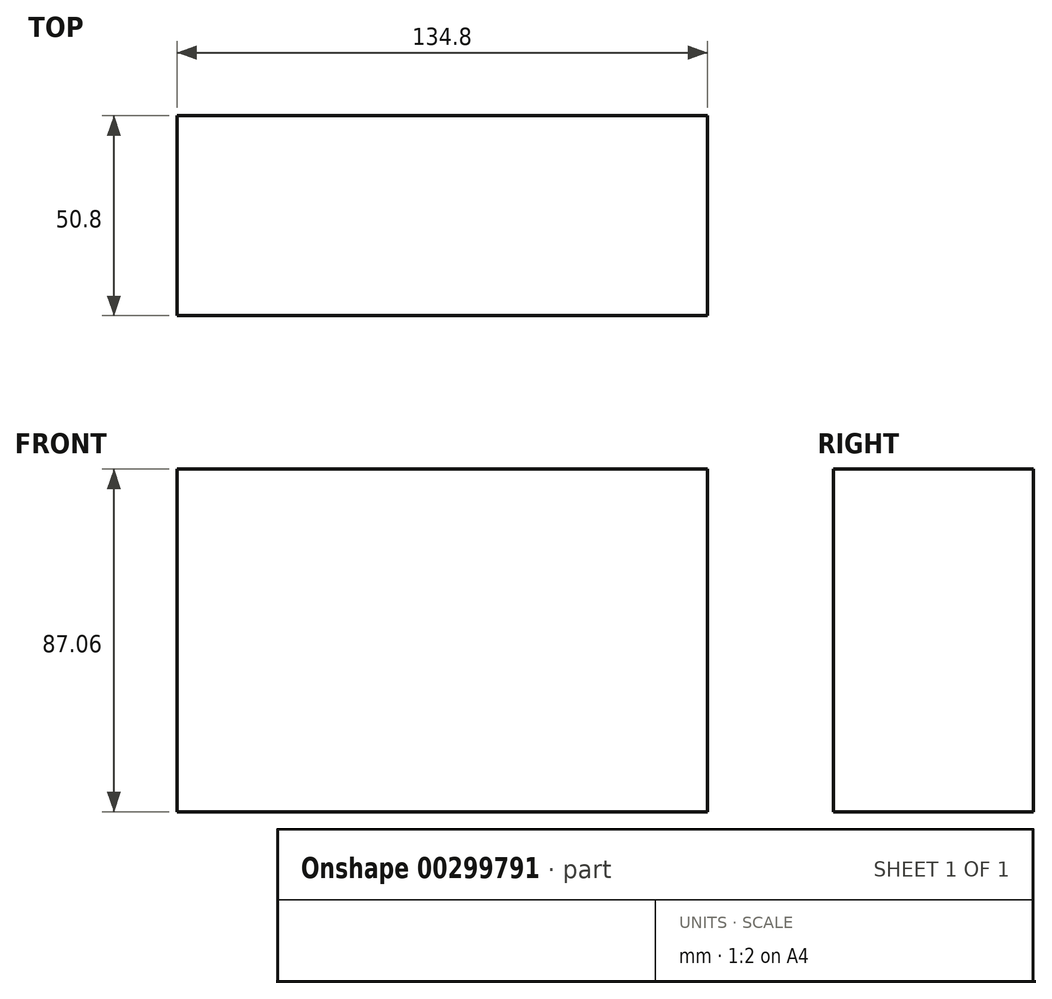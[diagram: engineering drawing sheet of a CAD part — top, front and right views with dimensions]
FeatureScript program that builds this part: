
annotation { "Feature Type Name" : "Feature", "Feature Type Description" : "" }
export const myFeature = defineFeature(function(context is Context, id is Id, definition is map)
    precondition{}
    {
        {
            var Q0;
            Q0=qCreatedBy(makeId("Front.planeOp"),FACE);
            var sketch = newSketch(context, id + "F0", { "sketchPlane" : qUnion([Q0])});
            skLineSegment(sketch, "E0.bottom", {"start": v(-52.6, 45.67) * mm, "end": v(82.2, 45.67) * mm});
            skLineSegment(sketch, "E0.top", {"start": v(-52.6, -41.4) * mm, "end": v(82.2, -41.4) * mm});
            skLineSegment(sketch, "E0.left", {"start": v(-52.6, 45.67) * mm, "end": v(-52.6, -41.4) * mm});
            skLineSegment(sketch, "E0.right", {"start": v(82.2, 45.67) * mm, "end": v(82.2, -41.4) * mm});
            skSolve(sketch);
        }
        {
            var Q0;
            Q0=makeQuery(id+"F0.imprint","IMPRINT",FACE,{"disambiguationData":[TD([[makeQuery(id+"F0.imprint","IMPRINT",EDGE,{"derivedFrom":sQuery(id+"F0.wireOp",EDGE,"E0.bottom")}),-1.0]])]});
            extrude(context, id + "F1", {"entities" : qUnion([Q0]), "depth" : 50.8 * mm});
        }
    });
